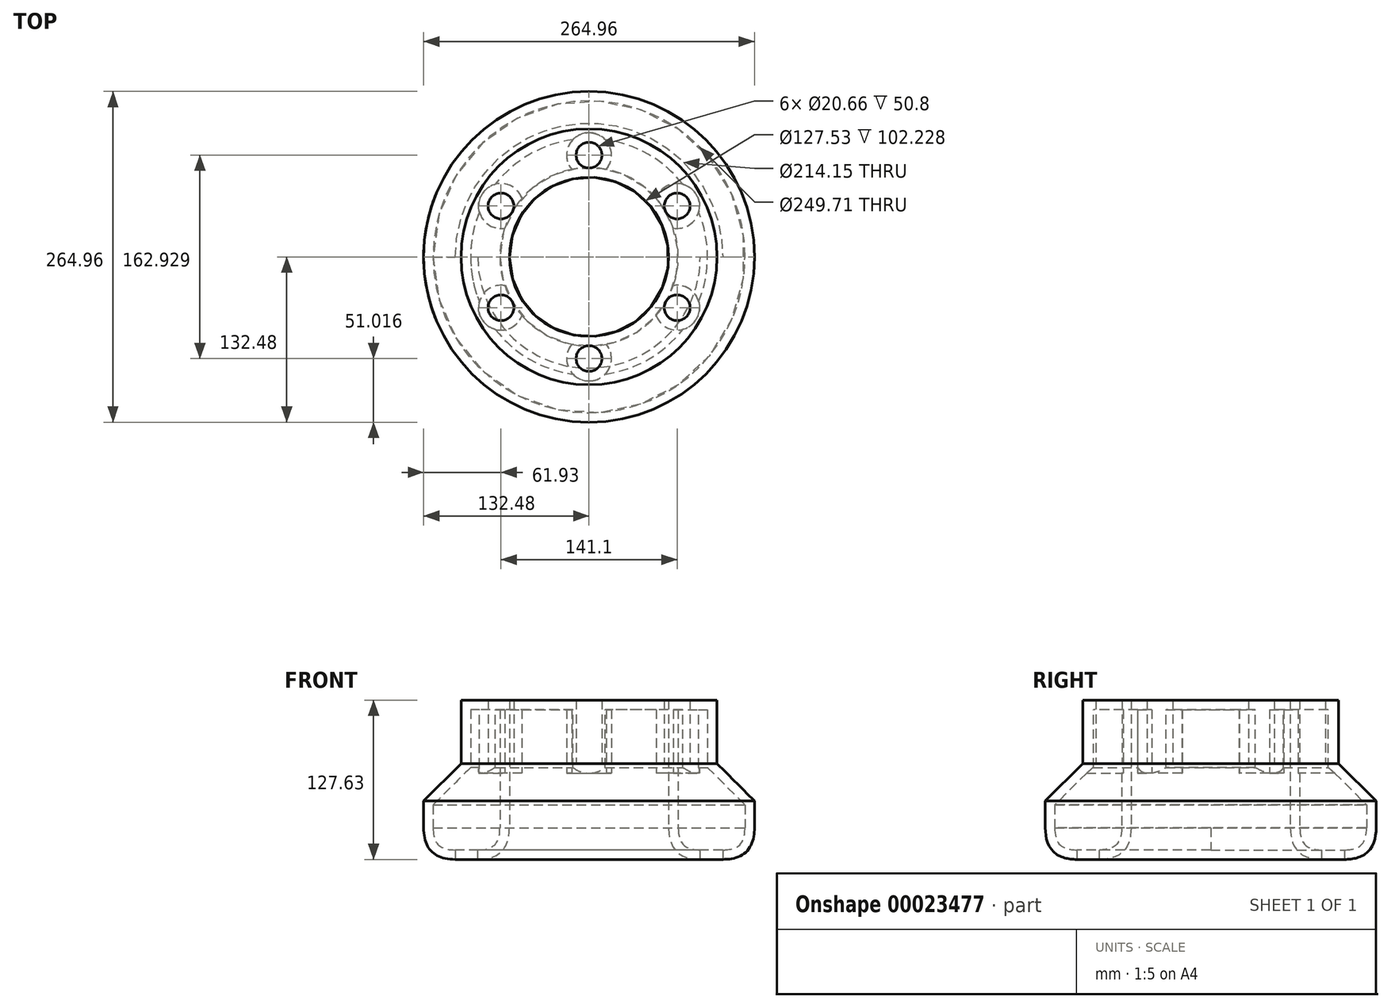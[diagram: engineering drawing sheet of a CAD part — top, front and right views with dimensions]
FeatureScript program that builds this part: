
annotation { "Feature Type Name" : "Feature", "Feature Type Description" : "" }
export const myFeature = defineFeature(function(context is Context, id is Id, definition is map)
    precondition{}
    {
        {
            var Q0;
            Q0=qCreatedBy(makeId("Front.planeOp"),FACE);
            var sketch = newSketch(context, id + "F0", { "sketchPlane" : qUnion([Q0])});
            skLineSegment(sketch, "E0.bottom", {"start": v(-132.48, 31.68) * mm, "end": v(-63.76, 31.68) * mm});
            skLineSegment(sketch, "E0.top", {"start": v(-132.48, -45.15) * mm, "end": v(-63.76, -45.15) * mm});
            skLineSegment(sketch, "E0.left", {"start": v(-132.48, 31.68) * mm, "end": v(-132.48, -45.15) * mm});
            skLineSegment(sketch, "E0.right", {"start": v(-63.76, 31.68) * mm, "end": v(-63.76, -45.15) * mm});
            skSolve(sketch);
        }
        {
            var Q0;
            Q0=qCreatedBy(makeId("Front.planeOp"),FACE);
            var sketch = newSketch(context, id + "F1", { "sketchPlane" : qUnion([Q0])});
            skLineSegment(sketch, "E1", {"start": v(0, 0) * mm, "end": v(0, 90.31) * mm});
            skSolve(sketch);
        }
        {
            var Q0;
            Q0=makeQuery(id+"F0.imprint","IMPRINT",FACE,{"disambiguationData":[TD([[makeQuery(id+"F0.imprint","IMPRINT",EDGE,{"derivedFrom":sQuery(id+"F0.wireOp",EDGE,"E0.bottom")}),-1.0]])]});
            var Q1;
            Q1=sQuery(id+"F1.wireOp",EDGE,"E1");
            revolve(context, id + "F2", {"entities" : qUnion([Q0]), "axis" : qUnion([Q1]), "revolveType" : RevolveType.FULL});
        }
        {
            var Q0;
            Q0=makeQuery(id+"F2.opRevolve","SWEPT_FACE",FACE,{"disambiguationData":[OSD([sQuery(id+"F0.wireOp",EDGE,"E0.top")])]});
            fillet(context, id + "F3", {"entities" : qUnion([Q0]), "radius" : 25.4 * mm, "tangentPropagation" : true, "rho" : 0.5, "crossSection" : FilletCrossSection.CONIC, "allowEdgeOverflow" : false});
        }
        {
            var Q0;
            Q0=makeQuery(id+"F2.opRevolve","SWEPT_EDGE",EDGE,{"disambiguationData":[OSD([sQuery(id+"F0.wireOp",EDGE,"E0.bottom"),sQuery(id+"F0.wireOp",EDGE,"E0.left")])]});
            chamfer(context, id + "F4", {"entities" : qUnion([Q0]), "width" : 30 * mm, "tangentPropagation" : true});
        }
        {
            var Q0;
            Q0=makeQuery(id+"F2.opRevolve","SWEPT_FACE",FACE,{"disambiguationData":[OSD([sQuery(id+"F0.wireOp",EDGE,"E0.bottom")])]});
            var sketch = newSketch(context, id + "F5", { "sketchPlane" : qUnion([Q0])});
            skCircle(sketch, "E2", {"center": v(0, 0) * mm, "radius": 81.46 * mm, "construction": true});
            skCircle(sketch, "E3", {"center": v(0, 81.46) * mm, "radius": 10.33 * mm});
            skCircle(sketch, "E4.1.0", {"center": v(-70.55, 40.73) * mm, "radius": 10.33 * mm});
            skCircle(sketch, "E4.2.0", {"center": v(-70.55, -40.73) * mm, "radius": 10.33 * mm});
            skCircle(sketch, "E4.3.0", {"center": v(0, -81.46) * mm, "radius": 10.33 * mm});
            skCircle(sketch, "E4.4.0", {"center": v(70.55, -40.73) * mm, "radius": 10.33 * mm});
            skCircle(sketch, "E4.5.0", {"center": v(70.55, 40.73) * mm, "radius": 10.33 * mm});
            skSolve(sketch);
        }
        {
            var Q0;
            Q0=makeQuery(id+"F5.imprint","IMPRINT",FACE,{"disambiguationData":[TD([[makeQuery(id+"F5.imprint","IMPRINT",EDGE,{"derivedFrom":sQuery(id+"F5.wireOp",EDGE,"E3")}),-1.0]])]});
            extrude(context, id + "F6", {"entities" : qUnion([Q0]), "operationType" : NewBodyOperationType.ADD, "depth" : 50.8 * mm});
        }
        {
            var Q0;
            Q0=makeQuery(id+"F2.opRevolve","SWEPT_FACE",FACE,{"disambiguationData":[OSD([sQuery(id+"F0.wireOp",EDGE,"E0.top")])]});
            shell(context, id + "F7", {"entities" : qUnion([Q0]), "thickness" : 7.62 * mm});
        }
    });
